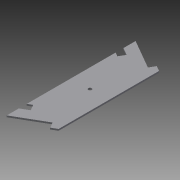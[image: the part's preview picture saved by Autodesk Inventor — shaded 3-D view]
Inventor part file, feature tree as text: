
AUTODESK INVENTOR PART (.ipt)
format: ipt  version: 2015 SP1 (Build 190203100, 203)  size: 125,952 bytes
history: native  units: in
note: dims shown in document units (in); Inventor stores cm internally (conversion verified against a paired STEP export)
features: reference x4, sketch x3, extrude x2, hole x1
ambient origin geometry x8: Origin, YZ Plane, XZ Plane, XY Plane, X Axis, Y Axis, Z Axis, Center Point
bodies: Solid1 (feature_tree)
feature tree (10):
  extrude  "Extrusion1"  TaperAngle=30.0deg  [1 undecoded]
  hole  "Hole1"  [1 undecoded]
  extrude  "Extrusion3"  Depth=3.0in
  sketch  "Sketch1"  dims[d0=120.0deg d1=30.0deg]
  sketch  "Sketch4"  dims[d2=16.0in d3=0.25in d4=0.0in]
  sketch  "Sketch5"  dims[d5=6.0in d12=3.0in d13=8.0in d14=0.5312in d15=0.75in d16=0.375in d17=0.25in d18=0.5635in d19=1.0in d20=0.8108in d22=0.04in d23=0.04in d24=0.04in d25=0.04in d26=1.0in d27=0.0in]
  reference  "Reference10"
  reference  "Reference11"
  reference  "Reference12"
  reference  "Reference13"
note: 2 required parameter values undecoded (feature->parameter linkage not recoverable at this tier; creation-order binding heuristic only, values carry confidence <= 0.55)
